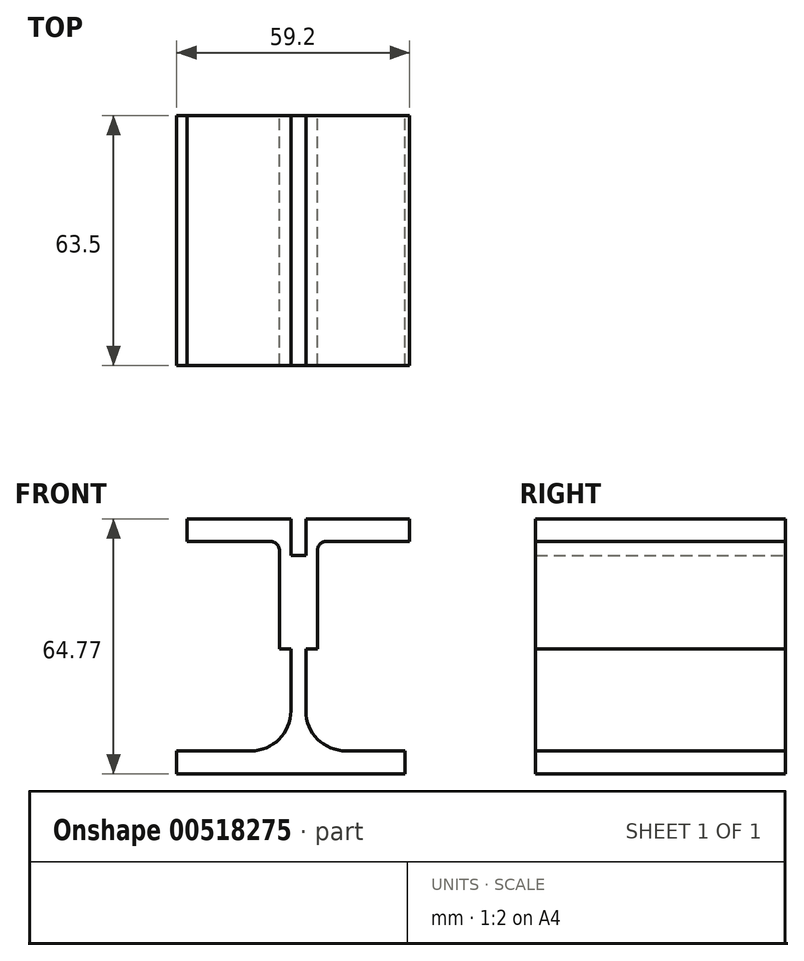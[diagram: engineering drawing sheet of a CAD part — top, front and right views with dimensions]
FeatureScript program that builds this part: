
annotation { "Feature Type Name" : "Feature", "Feature Type Description" : "" }
export const myFeature = defineFeature(function(context is Context, id is Id, definition is map)
    precondition{}
    {
        {
            var Q0;
            Q0=qCreatedBy(makeId("Front.planeOp"),FACE);
            var sketch = newSketch(context, id + "F0", { "sketchPlane" : qUnion([Q0])});
            skLineSegment(sketch, "E0.bottom", {"start": v(-65.3, 29.2) * mm, "end": v(-38.93, 29.2) * mm});
            skLineSegment(sketch, "E1.top", {"start": v(-38.93, -3.82) * mm, "end": v(-41.85, -3.82) * mm});
            skLineSegment(sketch, "E1.left", {"start": v(-38.93, 29.2) * mm, "end": v(-38.93, -3.82) * mm});
            skLineSegment(sketch, "E2.bottom", {"start": v(-67.95, -35.57) * mm, "end": v(-9.9, -35.57) * mm});
            skLineSegment(sketch, "E2.top", {"start": v(-67.95, -29.72) * mm, "end": v(-49.09, -29.72) * mm});
            skLineSegment(sketch, "E2.left", {"start": v(-67.95, -35.57) * mm, "end": v(-67.95, -29.72) * mm});
            skLineSegment(sketch, "E2.right", {"start": v(-9.9, -35.57) * mm, "end": v(-9.9, -29.72) * mm});
            skLineSegment(sketch, "E3.top", {"start": v(-38.93, 20) * mm, "end": v(-35.12, 20) * mm});
            skLineSegment(sketch, "E3.left", {"start": v(-38.93, -19.56) * mm, "end": v(-38.93, 20) * mm});
            skLineSegment(sketch, "E3.right", {"start": v(-35.12, -19.56) * mm, "end": v(-35.12, 20) * mm});
            skLineSegment(sketch, "E4", {"start": v(-65.3, 29.2) * mm, "end": v(-65.3, 23.49) * mm});
            skLineSegment(sketch, "E5", {"start": v(-41.85, 21.2) * mm, "end": v(-41.85, -3.82) * mm});
            skLineSegment(sketch, "E6", {"start": v(-44.13, 23.49) * mm, "end": v(-65.3, 23.49) * mm});
            skLineSegment(sketch, "E7", {"start": v(-35.12, 29.2) * mm, "end": v(-35.12, -3.82) * mm});
            skLineSegment(sketch, "E8", {"start": v(-35.12, -3.82) * mm, "end": v(-32.2, -3.82) * mm});
            skLineSegment(sketch, "E9", {"start": v(-32.2, -3.82) * mm, "end": v(-32.2, 21.2) * mm});
            skLineSegment(sketch, "E10", {"start": v(-29.9, 23.49) * mm, "end": v(-8.75, 23.49) * mm});
            skLineSegment(sketch, "E11", {"start": v(-8.75, 23.49) * mm, "end": v(-8.75, 29.2) * mm});
            skLineSegment(sketch, "E12", {"start": v(-8.75, 29.2) * mm, "end": v(-35.12, 29.2) * mm});
            skLineSegment(sketch, "E13.trimOffspring", {"start": v(-24.96, -29.72) * mm, "end": v(-9.9, -29.72) * mm});
            skPoint(sketch, "E14.visualSharp", {"position": v(-38.93, -29.72) * mm});
            skArc(sketch, "E14.filletArc", {"start": v(-49.09, -29.72) * mm, "mid": v(-41.9, -26.75) * mm, "end": v(-38.93, -19.56) * mm});
            skPoint(sketch, "E15.visualSharp", {"position": v(-35.12, -29.72) * mm});
            skArc(sketch, "E15.filletArc", {"start": v(-35.12, -19.56) * mm, "mid": v(-32.14, -26.75) * mm, "end": v(-24.96, -29.72) * mm});
            skPoint(sketch, "E16.visualSharp", {"position": v(-32.2, 23.49) * mm});
            skArc(sketch, "E16.filletArc", {"start": v(-29.9, 23.49) * mm, "mid": v(-31.53, 22.82) * mm, "end": v(-32.2, 21.2) * mm});
            skPoint(sketch, "E17.visualSharp", {"position": v(-41.85, 23.49) * mm});
            skArc(sketch, "E17.filletArc", {"start": v(-41.85, 21.2) * mm, "mid": v(-42.52, 22.82) * mm, "end": v(-44.13, 23.49) * mm});
            skSolve(sketch);
        }
        {
            var Q0;
            Q0=makeQuery(id+"F0.imprint","IMPRINT",FACE,{"disambiguationData":[TD([[makeQuery(id+"F0.imprint","IMPRINT",EDGE,{"derivedFrom":sQuery(id+"F0.wireOp",EDGE,"E0.bottom")}),-1.0]])]});
            var Q1;
            Q1=makeQuery(id+"F0.imprint","IMPRINT",FACE,{"disambiguationData":[TD([[makeQuery(id+"F0.imprint","IMPRINT",EDGE,{"derivedFrom":sQuery(id+"F0.wireOp",EDGE,"E2.bottom")}),1.0]])]});
            var Q2;
            {var subQ0=sQuery(id+"F0.wireOp",EDGE,"E8");Q2=makeQuery(id+"F0.imprint","IMPRINT",FACE,{"disambiguationData":[TD([[makeQuery(id+"F0.imprint","IMPRINT",EDGE,{"derivedFrom":subQ0}),1.0]])]});}
            extrude(context, id + "F1", {"entities" : qUnion([Q0, Q1, Q2]), "depth" : 63.5 * mm, "offsetDistance" : 25.4 * mm});
        }
    });
